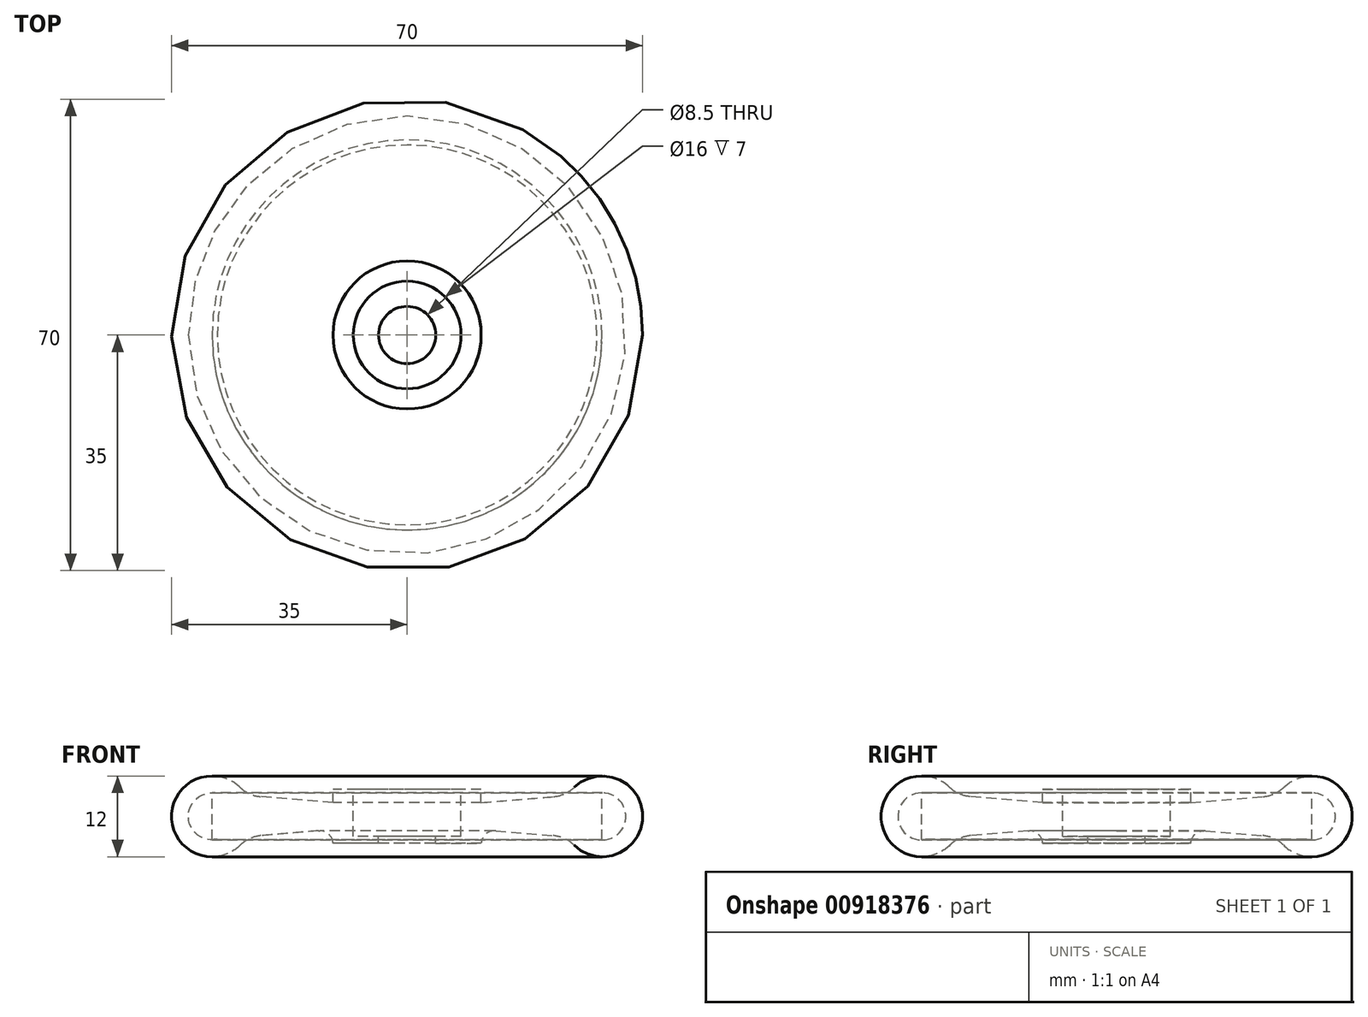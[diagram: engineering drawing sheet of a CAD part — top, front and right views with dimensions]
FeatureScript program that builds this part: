
annotation { "Feature Type Name" : "Feature", "Feature Type Description" : "" }
export const myFeature = defineFeature(function(context is Context, id is Id, definition is map)
    precondition{}
    {
        {
            var Q0;
            Q0=qCreatedBy(makeId("Front.planeOp"),FACE);
            var sketch = newSketch(context, id + "F0", { "sketchPlane" : qUnion([Q0])});
            skLineSegment(sketch, "E0", {"start": v(0, 0) * mm, "end": v(-29, 0) * mm});
            skCircle(sketch, "E1", {"center": v(-29, 0) * mm, "radius": 3.5 * mm});
            skCircle(sketch, "E2", {"center": v(-29, 0) * mm, "radius": 6 * mm});
            skSolve(sketch);
        }
        {
            var Q0;
            Q0=qCreatedBy(makeId("Front.planeOp"),FACE);
            var sketch = newSketch(context, id + "F1", { "sketchPlane" : qUnion([Q0])});
            skLineSegment(sketch, "E3", {"start": v(-28.97, 3.53) * mm, "end": v(-11, 2.04) * mm});
            skLineSegment(sketch, "E4", {"start": v(-28.97, -3.47) * mm, "end": v(-11, -1.96) * mm});
            skLineSegment(sketch, "E5", {"start": v(-28.97, 3.53) * mm, "end": v(-28.97, -3.47) * mm});
            skLineSegment(sketch, "E6", {"start": v(-11, 2.04) * mm, "end": v(-11, -1.96) * mm});
            skSolve(sketch);
        }
        {
            var Q0;
            Q0=qCreatedBy(makeId("Front.planeOp"),FACE);
            var sketch = newSketch(context, id + "F2", { "sketchPlane" : qUnion([Q0])});
            skLineSegment(sketch, "E7", {"start": v(0, 0) * mm, "end": v(-11, 0) * mm});
            skLineSegment(sketch, "E8", {"start": v(-11, 0) * mm, "end": v(-11, 4) * mm});
            skLineSegment(sketch, "E9", {"start": v(-11, 4) * mm, "end": v(-11, -4) * mm});
            skLineSegment(sketch, "E10", {"start": v(-11, -4) * mm, "end": v(-11, 4.02) * mm});
            skLineSegment(sketch, "E11", {"start": v(-11, 4.02) * mm, "end": v(0, 4.02) * mm});
            skLineSegment(sketch, "E12", {"start": v(0, 4.02) * mm, "end": v(0, -3.98) * mm});
            skLineSegment(sketch, "E13", {"start": v(0, -3.98) * mm, "end": v(-11, -4) * mm});
            skSolve(sketch);
        }
        {
            var Q0;
            Q0 = qSketchRegion(id + "F2", true);
            var Q1;
            Q1 = qSketchRegion(id + "F1", true);
            var Q2;
            Q2 = qSketchRegion(id + "F0", true);
            var Q3;
            Q3=sQuery(id+"F2.wireOp",EDGE,"E12");
            revolve(context, id + "F3", {"surfaceOperationType" : NewSurfaceOperationType.NEW, "entities" : qUnion([Q0, Q1, Q2]), "axis" : qUnion([Q3]), "revolveType" : RevolveType.FULL});
        }
        {
            var Q0;
            Q0=makeQuery(id+"F3.opRevolve","SWEPT_BODY",BODY,{"disambiguationData":[OSD([sQuery(id+"F0.wireOp",EDGE,"E1"),sQuery(id+"F0.wireOp",EDGE,"E2")])]});
            var Q1;
            Q1=makeQuery(id+"F3.opRevolve","SWEPT_BODY",BODY,{"disambiguationData":[OSD([sQuery(id+"F2.wireOp",EDGE,"E10"),sQuery(id+"F2.wireOp",EDGE,"E11"),sQuery(id+"F2.wireOp",EDGE,"E12"),sQuery(id+"F2.wireOp",EDGE,"E13")])]});
            var Q2;
            Q2=makeQuery(id+"F3.opRevolve","SWEPT_BODY",BODY,{"disambiguationData":[OSD([sQuery(id+"F1.wireOp",EDGE,"E3"),sQuery(id+"F1.wireOp",EDGE,"E4"),sQuery(id+"F1.wireOp",EDGE,"E5"),sQuery(id+"F1.wireOp",EDGE,"E6")])]});
            booleanBodies(context, id + "F4", {"operationType" : BooleanOperationType.UNION, "tools" : qUnion([Q0, Q1, Q2])});
        }
        {
            var Q0;
            Q0=makeQuery(id+"F4.opBoolean","INTERSECT",EDGE,{"derivedFrom":[makeQuery(id+"F3.opRevolve","SWEPT_FACE",FACE,{"disambiguationData":[OSD([sQuery(id+"F0.wireOp",EDGE,"E2")])]}),makeQuery(id+"F3.opRevolve","SWEPT_FACE",FACE,{"disambiguationData":[OSD([sQuery(id+"F1.wireOp",EDGE,"E3")])]})]});
            var Q1;
            Q1=makeQuery(id+"F4.opBoolean","INTERSECT",EDGE,{"derivedFrom":[makeQuery(id+"F3.opRevolve","SWEPT_FACE",FACE,{"disambiguationData":[OSD([sQuery(id+"F0.wireOp",EDGE,"E2")])]}),makeQuery(id+"F3.opRevolve","SWEPT_FACE",FACE,{"disambiguationData":[OSD([sQuery(id+"F1.wireOp",EDGE,"E4")])]})]});
            fillet(context, id + "F5", {"entities" : qUnion([Q0, Q1]), "radius" : 5 * mm, "tangentPropagation" : true, "allowEdgeOverflow" : false});
        }
        {
            var Q0;
            Q0=makeQuery(id+"F3.opRevolve","SWEPT_EDGE",EDGE,{"disambiguationData":[OSD([sQuery(id+"F1.wireOp",EDGE,"E3"),sQuery(id+"F1.wireOp",EDGE,"E6")])]});
            var Q1;
            Q1=makeQuery(id+"F3.opRevolve","SWEPT_EDGE",EDGE,{"disambiguationData":[OSD([sQuery(id+"F1.wireOp",EDGE,"E4"),sQuery(id+"F1.wireOp",EDGE,"E6")])]});
            fillet(context, id + "F6", {"entities" : qUnion([Q0, Q1]), "radius" : 2 * mm, "tangentPropagation" : true, "allowEdgeOverflow" : false});
        }
        {
            var Q0;
            Q0=makeQuery(id+"F3.opRevolve","SWEPT_FACE",FACE,{"disambiguationData":[OSD([sQuery(id+"F2.wireOp",EDGE,"E11")])]});
            var sketch = newSketch(context, id + "F7", { "sketchPlane" : qUnion([Q0])});
            skCircle(sketch, "E14", {"center": v(0, 0) * mm, "radius": 4.25 * mm});
            skSolve(sketch);
        }
        {
            var Q0;
            Q0=makeQuery(id+"F7.imprint","IMPRINT",FACE,{"disambiguationData":[TD([[makeQuery(id+"F7.imprint","IMPRINT",EDGE,{"derivedFrom":sQuery(id+"F7.wireOp",EDGE,"E14")}),1.0]])]});
            extrude(context, id + "F8", {"entities" : qUnion([Q0]), "operationType" : NewBodyOperationType.REMOVE, "endBound" : BoundingType.THROUGH_ALL, "oppositeDirection" : true, "depth" : 25 * mm, "offsetDistance" : 25 * mm});
        }
        {
            var Q0;
            Q0=makeQuery(id+"F3.opRevolve","SWEPT_FACE",FACE,{"disambiguationData":[OSD([sQuery(id+"F2.wireOp",EDGE,"E11")])]});
            var sketch = newSketch(context, id + "F9", { "sketchPlane" : qUnion([Q0])});
            skCircle(sketch, "E15", {"center": v(0, 0) * mm, "radius": 8 * mm});
            skSolve(sketch);
        }
        {
            var Q0;
            Q0=makeQuery(id+"F9.imprint","IMPRINT",FACE,{"disambiguationData":[TD([[makeQuery(id+"F9.imprint","IMPRINT",EDGE,{"derivedFrom":sQuery(id+"F9.wireOp",EDGE,"E15")}),1.0]])]});
            extrude(context, id + "F10", {"entities" : qUnion([Q0]), "operationType" : NewBodyOperationType.REMOVE, "oppositeDirection" : true, "depth" : 7 * mm, "offsetDistance" : 25 * mm});
        }
    });
